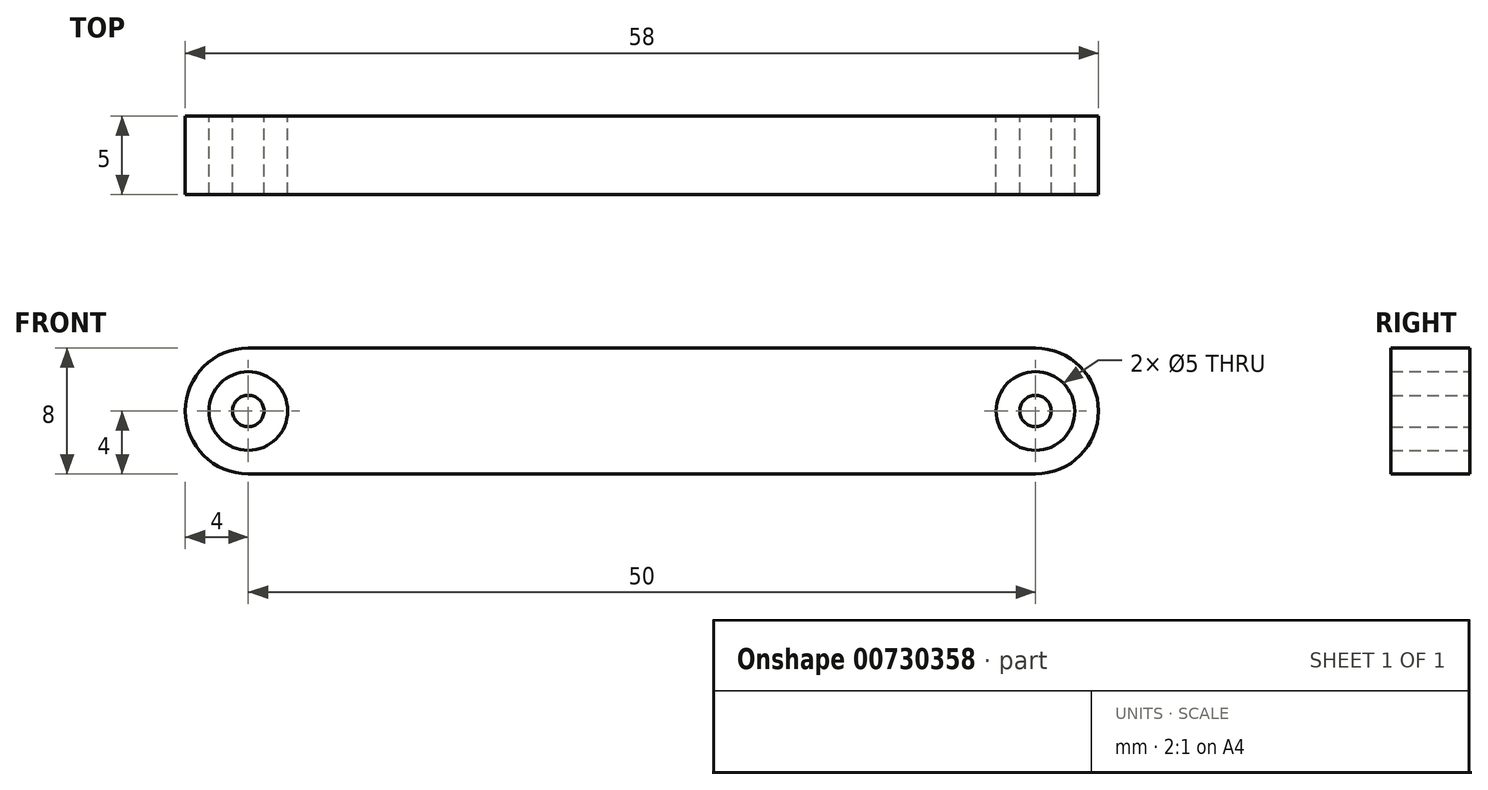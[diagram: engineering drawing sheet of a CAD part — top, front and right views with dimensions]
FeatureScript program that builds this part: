
annotation { "Feature Type Name" : "Feature", "Feature Type Description" : "" }
export const myFeature = defineFeature(function(context is Context, id is Id, definition is map)
    precondition{}
    {
        {
            var Q0;
            Q0=qCreatedBy(makeId("Front.planeOp"),FACE);
            var sketch = newSketch(context, id + "F0", { "sketchPlane" : qUnion([Q0])});
            skArc(sketch, "E0", {"start": v(0, 4) * mm, "mid": v(-4, 0) * mm, "end": v(0, -4) * mm});
            skCircle(sketch, "E1", {"center": v(0, 0) * mm, "radius": 2.5 * mm});
            skCircle(sketch, "E2", {"center": v(0, 0) * mm, "radius": 1 * mm});
            skArc(sketch, "E3", {"start": v(50, -4) * mm, "mid": v(54, 0) * mm, "end": v(50, 4) * mm});
            skCircle(sketch, "E4", {"center": v(50, 0) * mm, "radius": 2.5 * mm});
            skCircle(sketch, "E5", {"center": v(50, 0) * mm, "radius": 1 * mm});
            skLineSegment(sketch, "E6", {"start": v(0, 4) * mm, "end": v(50, 4) * mm});
            skLineSegment(sketch, "E7", {"start": v(0, -4) * mm, "end": v(50, -4) * mm});
            skSolve(sketch);
        }
        {
            var Q0;
            Q0 = qSketchRegion(id + "F0", true);
            var Q1;
            Q1=makeQuery(id+"F0.imprint","IMPRINT",FACE,{"disambiguationData":[TD([[makeQuery(id+"F0.imprint","IMPRINT",EDGE,{"derivedFrom":sQuery(id+"F0.wireOp",EDGE,"E2")}),1.0]])]});
            var Q2;
            Q2=makeQuery(id+"F0.imprint","IMPRINT",FACE,{"disambiguationData":[TD([[makeQuery(id+"F0.imprint","IMPRINT",EDGE,{"derivedFrom":sQuery(id+"F0.wireOp",EDGE,"E5")}),1.0]])]});
            extrude(context, id + "F1", {"entities" : qUnion([Q0, Q1, Q2]), "depth" : 5 * mm, "offsetDistance" : 25 * mm});
        }
    });
